# Revit family: VICTRIX PRO 55 ErP
name_source: partatom
category: Modelli generici
revit_build: Autodesk Revit 2017 (Build: 20160225_1515(x64)
units: mm (PartAtom-declared; Revit-internal decimal feet)

## family parameters
Basato su piano di lavoro = No
Condiviso = No
Punto di calcolo locali = No
Può ospitare armatura = No
Quota connettore circolare = Usa diametro
Sempre verticale = Sì
Taglio con vuoti quando caricato = No
Tipo di parte = Normale

## types (1)
- VICTRIX PRO 55 ErP
    Altezza totale = 843 mm  [stored 2.76575 ft]
    Assorbimento nominale = 0,95 A
    BC_OBJECT_ID = 8367
    BC_OBJECT_VERSION = #1
    BC_VARIANT_ID = 25528
    Capacità di acqua della caldiaia = 0 m³
    Codice Uniformat = D3020
    Codice prodotto = 3.025612
    Collegamenti Idraulici = 2 mm  [stored 0.00656168 ft]
    Corrente Nominale = 1 A
    Data di creazione = 12/10/2017 17:22:28
    Descrizione = Caldaia murale modulare a condensazione, ad alta potenza
    Diametro attacco GAS = 19 mm
    Diametro collegamento fumi = 80 mm  [stored 0.262467 ft]
    Dimensioni di Collegamento Tubature = 19 mm
    Frequenza di utilizzo = 50 Hz
    Grado di isolamento elettrico = X5D
    IfcExportAs = IfcBoilerType
    Larghezza Totale = 450 mm  [stored 1.47638 ft]
    Link dell'oggetto sul sito del produttore = https://www.immergas.com
    Massa = 51.40 kg
    MasterFormat = 23 00 00- Heating, Ventilating, and Air Conditioning (HVAC)
    Modello = VICTRIX PRO 55 ErP
    Nome BIM&CO = Caldaia
    NominalHeight = 843 mm  [stored 2.76575 ft]
    NominalWidth = 450 mm  [stored 1.47638 ft]
    Oggetto dell'autore = Bim&Co Italia
    Portata termica = 51300 W
    Portata termica nominale massima = 51,3 (44.098) kW (kcal/h)
    Portata termica nominale minima = 5,5 (4.715 )kW (kcal/h)
    Potenza elettrica prodotta = 155000 W
    Potenza termica a 80/60°C = 49900 W
    Prevalenza disponibile con portata 1000 l/h = 70,1 (7,13) kPa (m c.a.)
    Produttore = Immergas
    Profondità Totale = 457 mm  [stored 1.49934 ft]
    Rendimento a carico nominale 100% Pn (%) = 97.3
    Rendimento a carico nominale 30% Pn (%) = 101.1
    Rendimento utile al 100 % della potenza = >93+2·log Pn
    Temperatura di esercizio = 90 °C
    Temperatura regolabile impianto riscaldamento = 20-85 °C
    Tipo di oggetto = HVAC
    URL Autore = https://www.bimandco.com
    Uniformat = Heat Generating Systems
    Voltaggio Nominale = 230 V

note: [stored X ft] marks values corroborated as IEEE doubles in the binary element streams (Revit-internal decimal feet)
